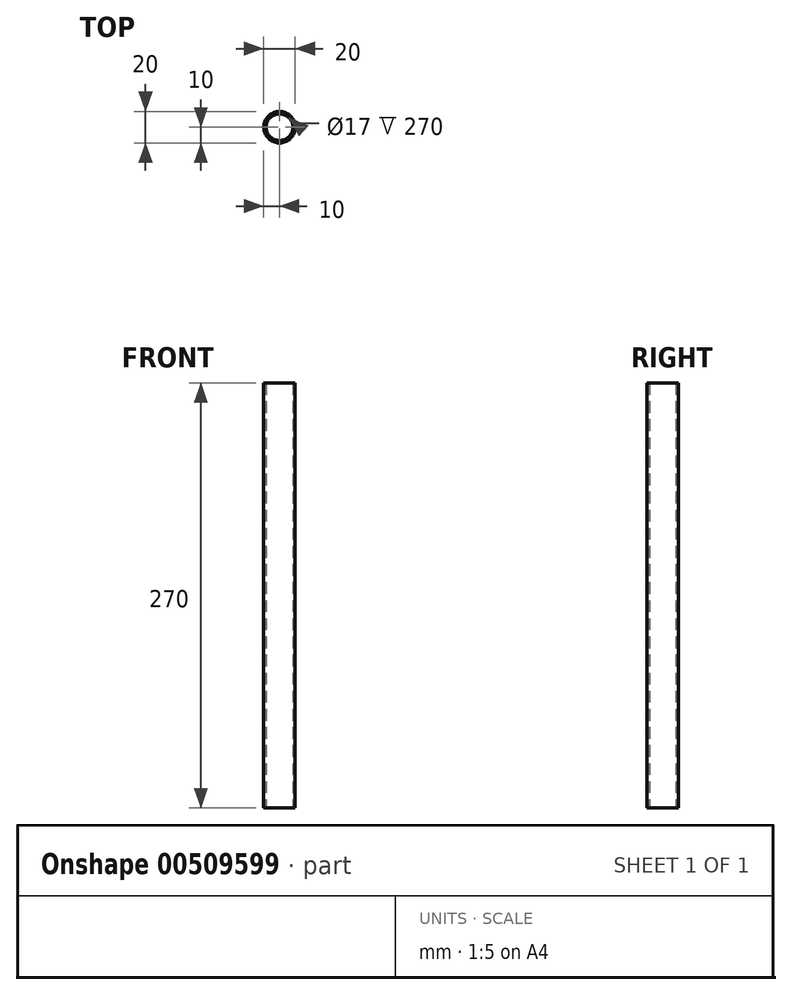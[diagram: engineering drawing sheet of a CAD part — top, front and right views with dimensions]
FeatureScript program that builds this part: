
annotation { "Feature Type Name" : "Feature", "Feature Type Description" : "" }
export const myFeature = defineFeature(function(context is Context, id is Id, definition is map)
    precondition{}
    {
        {
            var Q0;
            Q0=qCreatedBy(makeId("Top.planeOp"),FACE);
            var sketch = newSketch(context, id + "F0", { "sketchPlane" : qUnion([Q0])});
            skCircle(sketch, "E0", {"center": v(0, 0) * mm, "radius": 10 * mm});
            skCircle(sketch, "E1.0", {"center": v(0, 0) * mm, "radius": 8.5 * mm});
            skSolve(sketch);
        }
        {
            var Q0;
            Q0=makeQuery(id+"F0.imprint","IMPRINT",FACE,{"disambiguationData":[TD([[makeQuery(id+"F0.imprint","IMPRINT",EDGE,{"derivedFrom":sQuery(id+"F0.wireOp",EDGE,"E0")}),1.0]])]});
            extrude(context, id + "F1", {"entities" : qUnion([Q0]), "depth" : 270 * mm, "offsetDistance" : 25 * mm});
        }
    });
